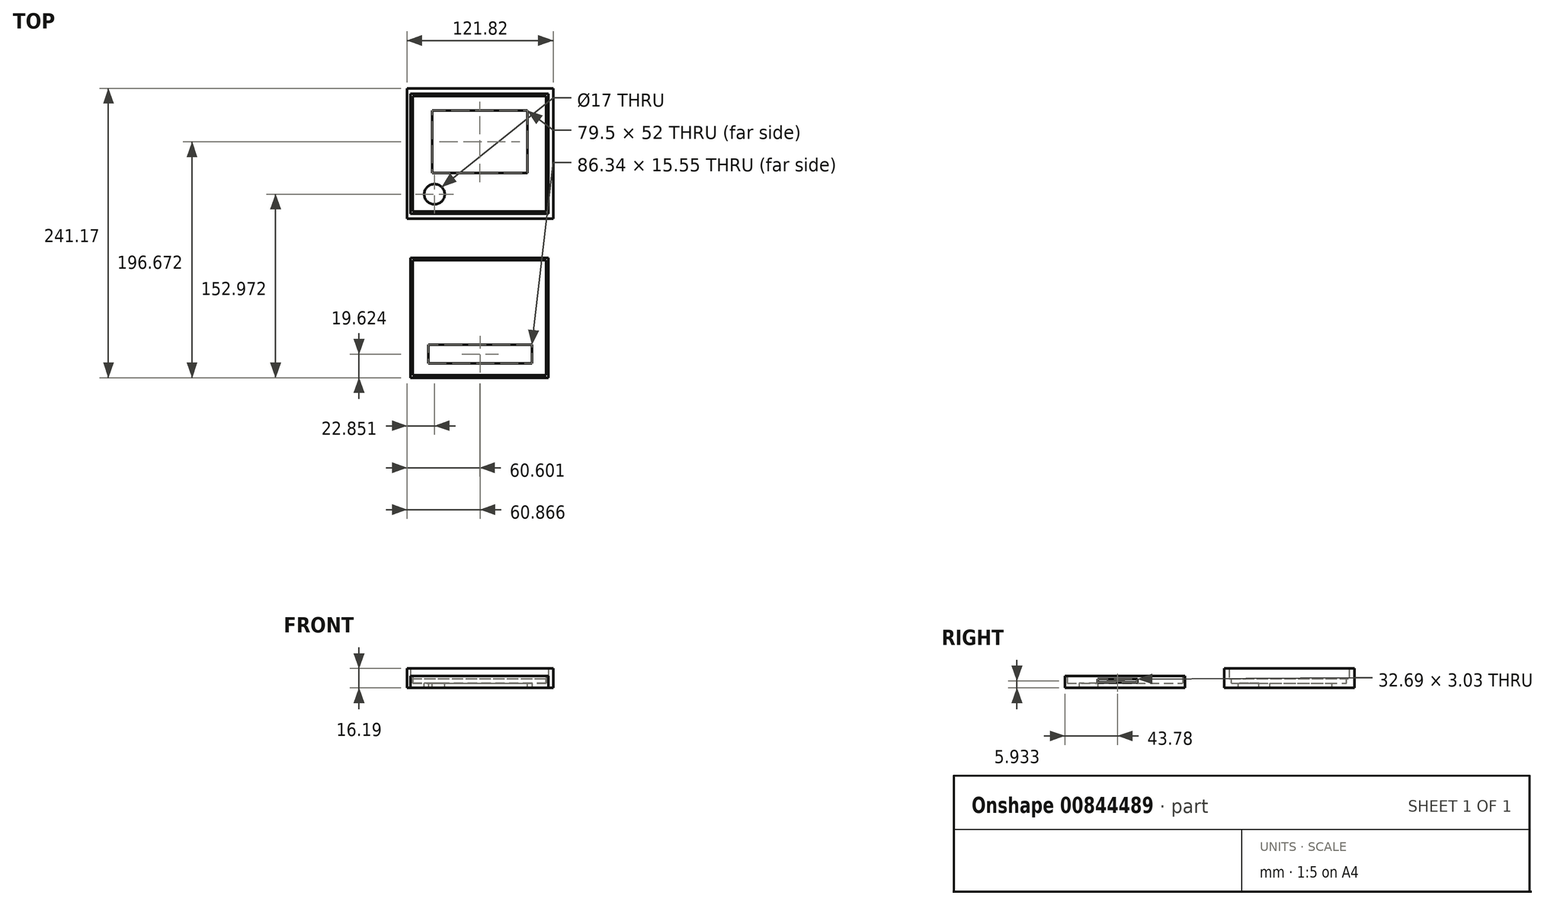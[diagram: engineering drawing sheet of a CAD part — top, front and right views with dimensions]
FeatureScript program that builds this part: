
annotation { "Feature Type Name" : "Feature", "Feature Type Description" : "" }
export const myFeature = defineFeature(function(context is Context, id is Id, definition is map)
    precondition{}
    {
        {
            var Q0;
            Q0=qCreatedBy(makeId("Top.planeOp"),FACE);
            var sketch = newSketch(context, id + "F0", { "sketchPlane" : qUnion([Q0])});
            skLineSegment(sketch, "E0.bottom", {"start": v(-57.57, 49.99) * mm, "end": v(57.43, 49.99) * mm});
            skLineSegment(sketch, "E0.top", {"start": v(-57.57, -50.01) * mm, "end": v(57.43, -50.01) * mm});
            skLineSegment(sketch, "E0.left", {"start": v(-57.57, 49.99) * mm, "end": v(-57.57, -50.01) * mm});
            skLineSegment(sketch, "E0.right", {"start": v(57.43, 49.99) * mm, "end": v(57.43, -50.01) * mm});
            skPoint(sketch, "E1", {"position": v(-0.07, 49.99) * mm});
            skPoint(sketch, "E2", {"position": v(57.43, -0.01) * mm});
            skLineSegment(sketch, "E3.bottom", {"start": v(-55.57, 47.99) * mm, "end": v(55.43, 47.99) * mm});
            skLineSegment(sketch, "E3.top", {"start": v(-55.57, -48.01) * mm, "end": v(55.43, -48.01) * mm});
            skLineSegment(sketch, "E3.left", {"start": v(-55.57, 47.99) * mm, "end": v(-55.57, -48.01) * mm});
            skLineSegment(sketch, "E3.right", {"start": v(55.43, 47.99) * mm, "end": v(55.43, -48.01) * mm});
            skSolve(sketch);
        }
        {
            var Q0;
            Q0=makeQuery(id+"F0.imprint","IMPRINT",FACE,{"disambiguationData":[TD([[makeQuery(id+"F0.imprint","IMPRINT",EDGE,{"derivedFrom":sQuery(id+"F0.wireOp",EDGE,"E3.bottom")}),-1.0]])]});
            var Q1;
            Q1=makeQuery(id+"F0.imprint","IMPRINT",FACE,{"disambiguationData":[TD([[makeQuery(id+"F0.imprint","IMPRINT",EDGE,{"derivedFrom":sQuery(id+"F0.wireOp",EDGE,"E0.bottom")}),-1.0]])]});
            extrude(context, id + "F1", {"entities" : qUnion([Q0, Q1]), "depth" : 4 * mm, "offsetDistance" : 25.4 * mm});
        }
        {
            var Q0;
            Q0=makeQuery(id+"F0.imprint","IMPRINT",FACE,{"disambiguationData":[TD([[makeQuery(id+"F0.imprint","IMPRINT",EDGE,{"derivedFrom":sQuery(id+"F0.wireOp",EDGE,"E0.bottom")}),-1.0]])]});
            extrude(context, id + "F2", {"entities" : qUnion([Q0]), "operationType" : NewBodyOperationType.ADD, "depth" : 10 * mm, "offsetDistance" : 25.4 * mm});
        }
        {
            var Q0;
            Q0=makeQuery(id+"F1.opExtrude","CAP_FACE",FACE,{"disambiguationData":[OSD([sQuery(id+"F0.wireOp",EDGE,"E0.bottom"),sQuery(id+"F0.wireOp",EDGE,"E0.top"),sQuery(id+"F0.wireOp",EDGE,"E0.left"),sQuery(id+"F0.wireOp",EDGE,"E0.right")])],"isStart":true});
            var sketch = newSketch(context, id + "F3", { "sketchPlane" : qUnion([Q0])});
            skLineSegment(sketch, "E4.bottom", {"start": v(-42.7, 38.16) * mm, "end": v(43.64, 38.16) * mm});
            skLineSegment(sketch, "E4.top", {"start": v(-42.7, 22.6) * mm, "end": v(43.64, 22.6) * mm});
            skLineSegment(sketch, "E4.left", {"start": v(-42.7, 38.16) * mm, "end": v(-42.7, 22.6) * mm});
            skLineSegment(sketch, "E4.right", {"start": v(43.64, 38.16) * mm, "end": v(43.64, 22.6) * mm});
            skSolve(sketch);
        }
        {
            var Q0;
            Q0=makeQuery(id+"F3.imprint","IMPRINT",FACE,{"disambiguationData":[TD([[makeQuery(id+"F3.imprint","IMPRINT",EDGE,{"derivedFrom":sQuery(id+"F3.wireOp",EDGE,"E4.bottom")}),-1.0]])]});
            extrude(context, id + "F4", {"entities" : qUnion([Q0]), "operationType" : NewBodyOperationType.REMOVE, "oppositeDirection" : true, "depth" : 25.4 * mm, "offsetDistance" : 25.4 * mm});
        }
        {
            var Q0;
            {var subQ0=sQuery(id+"F0.wireOp",EDGE,"E0.right");Q0=makeQuery(id+"F2.boolean.opBoolean","MERGE",FACE,{"derivedFrom":[makeQuery(id+"F1.opExtrude","SWEPT_FACE",FACE,{"disambiguationData":[OSD([subQ0])]}),makeQuery(id+"F2.opExtrude","SWEPT_FACE",FACE,{"disambiguationData":[OSD([subQ0])]})]});}
            var sketch = newSketch(context, id + "F5", { "sketchPlane" : qUnion([Q0])});
            skLineSegment(sketch, "E5.bottom", {"start": v(-22.58, 7.42) * mm, "end": v(10.12, 7.42) * mm});
            skLineSegment(sketch, "E5.top", {"start": v(-22.58, 4.39) * mm, "end": v(10.12, 4.39) * mm});
            skLineSegment(sketch, "E5.left", {"start": v(-22.58, 7.42) * mm, "end": v(-22.58, 4.39) * mm});
            skLineSegment(sketch, "E5.right", {"start": v(10.12, 7.42) * mm, "end": v(10.12, 4.39) * mm});
            skSolve(sketch);
        }
        {
            var Q0;
            Q0=makeQuery(id+"F5.imprint","IMPRINT",FACE,{"disambiguationData":[TD([[makeQuery(id+"F5.imprint","IMPRINT",EDGE,{"derivedFrom":sQuery(id+"F5.wireOp",EDGE,"E5.bottom")}),-1.0]])]});
            extrude(context, id + "F6", {"entities" : qUnion([Q0]), "operationType" : NewBodyOperationType.REMOVE, "oppositeDirection" : true, "depth" : 30.23 * mm, "offsetDistance" : 25.4 * mm, "hasSecondDirection" : true, "secondDirectionOppositeDirection" : false, "secondDirectionDepth" : 19.68 * mm});
        }
        {
            var Q0;
            Q0=makeQuery(id+"F2.opExtrude","CAP_FACE",FACE,{"disambiguationData":[OSD([sQuery(id+"F0.wireOp",EDGE,"E0.bottom"),sQuery(id+"F0.wireOp",EDGE,"E0.top"),sQuery(id+"F0.wireOp",EDGE,"E0.left"),sQuery(id+"F0.wireOp",EDGE,"E0.right"),sQuery(id+"F0.wireOp",EDGE,"E3.bottom"),sQuery(id+"F0.wireOp",EDGE,"E3.top"),sQuery(id+"F0.wireOp",EDGE,"E3.left"),sQuery(id+"F0.wireOp",EDGE,"E3.right")])],"isStart":false});
            var sketch = newSketch(context, id + "F7", { "sketchPlane" : qUnion([Q0])});
            skLineSegment(sketch, "E6.bottom", {"start": v(-57.57, 49.99) * mm, "end": v(57.43, 49.99) * mm});
            skLineSegment(sketch, "E6.top", {"start": v(-57.57, -50.01) * mm, "end": v(57.43, -50.01) * mm});
            skLineSegment(sketch, "E6.left", {"start": v(-57.57, 49.99) * mm, "end": v(-57.57, -50.01) * mm});
            skLineSegment(sketch, "E6.right", {"start": v(57.43, 49.99) * mm, "end": v(57.43, -50.01) * mm});
            skLineSegment(sketch, "E7.bottom", {"start": v(-60.39, 53.99) * mm, "end": v(61.43, 53.99) * mm});
            skLineSegment(sketch, "E7.top", {"start": v(-60.39, -54.46) * mm, "end": v(61.43, -54.46) * mm});
            skLineSegment(sketch, "E7.left", {"start": v(-60.39, 53.99) * mm, "end": v(-60.39, -54.46) * mm});
            skLineSegment(sketch, "E7.right", {"start": v(61.43, 53.99) * mm, "end": v(61.43, -54.46) * mm});
            skSolve(sketch);
        }
        {
            var Q0;
            Q0=makeQuery(id+"F7.imprint","IMPRINT",FACE,{"disambiguationData":[TD([[makeQuery(id+"F7.imprint","IMPRINT",EDGE,{"derivedFrom":sQuery(id+"F7.wireOp",EDGE,"E6.bottom")}),1.0]])]});
            extrude(context, id + "F8", {"entities" : qUnion([Q0]), "oppositeDirection" : true, "depth" : 8.38 * mm, "offsetDistance" : 25.4 * mm});
        }
        {
            var Q0;
            Q0=makeQuery(id+"F8.opExtrude","CAP_FACE",FACE,{"disambiguationData":[OSD([sQuery(id+"F7.wireOp",EDGE,"E6.bottom"),sQuery(id+"F7.wireOp",EDGE,"E6.top"),sQuery(id+"F7.wireOp",EDGE,"E6.left"),sQuery(id+"F7.wireOp",EDGE,"E6.right"),sQuery(id+"F7.wireOp",EDGE,"E7.bottom"),sQuery(id+"F7.wireOp",EDGE,"E7.top"),sQuery(id+"F7.wireOp",EDGE,"E7.left"),sQuery(id+"F7.wireOp",EDGE,"E7.right")])],"isStart":true});
            var Q1;
            Q1=makeQuery(id+"F2.opExtrude","CAP_FACE",FACE,{"disambiguationData":[OSD([sQuery(id+"F0.wireOp",EDGE,"E0.bottom"),sQuery(id+"F0.wireOp",EDGE,"E0.top"),sQuery(id+"F0.wireOp",EDGE,"E0.left"),sQuery(id+"F0.wireOp",EDGE,"E0.right"),sQuery(id+"F0.wireOp",EDGE,"E3.bottom"),sQuery(id+"F0.wireOp",EDGE,"E3.top"),sQuery(id+"F0.wireOp",EDGE,"E3.left"),sQuery(id+"F0.wireOp",EDGE,"E3.right")])],"isStart":false});
            extrude(context, id + "F9", {"entities" : qUnion([Q0, Q1]), "depth" : 3.8 * mm, "offsetDistance" : 25.4 * mm});
        }
        {
            var Q0;
            Q0=makeQuery(id+"F9.opExtrude","SWEPT_BODY",BODY,{"disambiguationData":[OSD([sQuery(id+"F7.wireOp",EDGE,"E6.bottom"),sQuery(id+"F7.wireOp",EDGE,"E6.top"),sQuery(id+"F7.wireOp",EDGE,"E6.left"),sQuery(id+"F7.wireOp",EDGE,"E6.right"),sQuery(id+"F7.wireOp",EDGE,"E7.bottom"),sQuery(id+"F7.wireOp",EDGE,"E7.top"),sQuery(id+"F7.wireOp",EDGE,"E7.left"),sQuery(id+"F7.wireOp",EDGE,"E7.right")])]});
            var Q1;
            Q1=makeQuery(id+"F9.opExtrude","SWEPT_BODY",BODY,{"disambiguationData":[OSD([sQuery(id+"F0.wireOp",EDGE,"E0.bottom"),sQuery(id+"F0.wireOp",EDGE,"E0.top"),sQuery(id+"F0.wireOp",EDGE,"E0.left"),sQuery(id+"F0.wireOp",EDGE,"E0.right"),sQuery(id+"F0.wireOp",EDGE,"E3.bottom"),sQuery(id+"F0.wireOp",EDGE,"E3.top"),sQuery(id+"F0.wireOp",EDGE,"E3.left"),sQuery(id+"F0.wireOp",EDGE,"E3.right")])]});
            var Q2;
            Q2=makeQuery(id+"F8.opExtrude","SWEPT_BODY",BODY,{"disambiguationData":[OSD([sQuery(id+"F7.wireOp",EDGE,"E6.bottom"),sQuery(id+"F7.wireOp",EDGE,"E6.top"),sQuery(id+"F7.wireOp",EDGE,"E6.left"),sQuery(id+"F7.wireOp",EDGE,"E6.right"),sQuery(id+"F7.wireOp",EDGE,"E7.bottom"),sQuery(id+"F7.wireOp",EDGE,"E7.top"),sQuery(id+"F7.wireOp",EDGE,"E7.left"),sQuery(id+"F7.wireOp",EDGE,"E7.right")])]});
            booleanBodies(context, id + "F10", {"operationType" : BooleanOperationType.UNION, "tools" : qUnion([Q0, Q1, Q2])});
        }
        {
            var Q0;
            Q0=makeQuery(id+"F10.opBoolean","MERGE",FACE,{"derivedFrom":[makeQuery(id+"F9.opExtrude","CAP_FACE",FACE,{"disambiguationData":[OSD([sQuery(id+"F0.wireOp",EDGE,"E0.bottom"),sQuery(id+"F0.wireOp",EDGE,"E0.top"),sQuery(id+"F0.wireOp",EDGE,"E0.left"),sQuery(id+"F0.wireOp",EDGE,"E0.right"),sQuery(id+"F0.wireOp",EDGE,"E3.bottom"),sQuery(id+"F0.wireOp",EDGE,"E3.top"),sQuery(id+"F0.wireOp",EDGE,"E3.left"),sQuery(id+"F0.wireOp",EDGE,"E3.right")])],"isStart":false}),makeQuery(id+"F9.opExtrude","CAP_FACE",FACE,{"disambiguationData":[OSD([sQuery(id+"F7.wireOp",EDGE,"E6.bottom"),sQuery(id+"F7.wireOp",EDGE,"E6.top"),sQuery(id+"F7.wireOp",EDGE,"E6.left"),sQuery(id+"F7.wireOp",EDGE,"E6.right"),sQuery(id+"F7.wireOp",EDGE,"E7.bottom"),sQuery(id+"F7.wireOp",EDGE,"E7.top"),sQuery(id+"F7.wireOp",EDGE,"E7.left"),sQuery(id+"F7.wireOp",EDGE,"E7.right")])],"isStart":false})]});
            var sketch = newSketch(context, id + "F11", { "sketchPlane" : qUnion([Q0])});
            skLineSegment(sketch, "E8.bottom", {"start": v(-39.54, 16.04) * mm, "end": v(39.96, 16.04) * mm});
            skLineSegment(sketch, "E8.top", {"start": v(-39.54, -35.96) * mm, "end": v(39.96, -35.96) * mm});
            skLineSegment(sketch, "E8.left", {"start": v(-39.54, 16.04) * mm, "end": v(-39.54, -35.96) * mm});
            skLineSegment(sketch, "E8.right", {"start": v(39.96, 16.04) * mm, "end": v(39.96, -35.96) * mm});
            skCircle(sketch, "E9", {"center": v(-37.54, 33.74) * mm, "radius": 8.5 * mm});
            skSolve(sketch);
        }
        {
            var Q0;
            Q0=makeQuery(id+"F11.imprint","IMPRINT",FACE,{"disambiguationData":[TD([[makeQuery(id+"F11.imprint","IMPRINT",EDGE,{"derivedFrom":sQuery(id+"F11.wireOp",EDGE,"E8.bottom")}),1.0]])]});
            var Q1;
            Q1=makeQuery(id+"F11.imprint","IMPRINT",FACE,{"disambiguationData":[TD([[makeQuery(id+"F11.imprint","IMPRINT",EDGE,{"derivedFrom":makeQuery(id+"F9.opExtrude","CAP_EDGE",EDGE,{"disambiguationData":[OSD([sQuery(id+"F0.wireOp",EDGE,"E3.bottom")])],"isStart":false})}),1.0]])]});
            extrude(context, id + "F12", {"entities" : qUnion([Q0, Q1]), "operationType" : NewBodyOperationType.ADD, "depth" : 4 * mm, "offsetDistance" : 25.4 * mm});
        }
        {
            var Q0;
            Q0=qCreatedBy(makeId("Top.planeOp"),FACE);
            var sketch = newSketch(context, id + "F13", { "sketchPlane" : qUnion([Q0])});
            skLineSegment(sketch, "E10", {"start": v(-72.14, 68.35) * mm, "end": v(70.81, 68.35) * mm});
            skSolve(sketch);
        }
        {
            var Q0;
            Q0=makeQuery(id+"F9.opExtrude","SWEPT_BODY",BODY,{"disambiguationData":[OSD([sQuery(id+"F7.wireOp",EDGE,"E6.bottom"),sQuery(id+"F7.wireOp",EDGE,"E6.top"),sQuery(id+"F7.wireOp",EDGE,"E6.left"),sQuery(id+"F7.wireOp",EDGE,"E6.right"),sQuery(id+"F7.wireOp",EDGE,"E7.bottom"),sQuery(id+"F7.wireOp",EDGE,"E7.top"),sQuery(id+"F7.wireOp",EDGE,"E7.left"),sQuery(id+"F7.wireOp",EDGE,"E7.right")])]});
            var Q1;
            Q1=sQuery(id+"F13.wireOp",EDGE,"E10");
            transform(context, id + "F14", {"entities" : qUnion([Q0]), "transformType" : TransformType.ROTATION, "transformAxis" : qUnion([Q1]), "angle" : 180 * degree, "oppositeDirection" : true, "makeCopy" : false});
        }
        {
            var Q0;
            Q0=makeQuery(id+"F9.opExtrude","SWEPT_BODY",BODY,{"disambiguationData":[OSD([sQuery(id+"F7.wireOp",EDGE,"E6.bottom"),sQuery(id+"F7.wireOp",EDGE,"E6.top"),sQuery(id+"F7.wireOp",EDGE,"E6.left"),sQuery(id+"F7.wireOp",EDGE,"E6.right"),sQuery(id+"F7.wireOp",EDGE,"E7.bottom"),sQuery(id+"F7.wireOp",EDGE,"E7.top"),sQuery(id+"F7.wireOp",EDGE,"E7.left"),sQuery(id+"F7.wireOp",EDGE,"E7.right")])]});
            transform(context, id + "F15", {"entities" : qUnion([Q0]), "transformType" : TransformType.TRANSLATION_3D, "dx" : 0 * mm, "dy" : 0 * mm, "dz" : 17.78 * mm, "makeCopy" : false});
        }
    });
